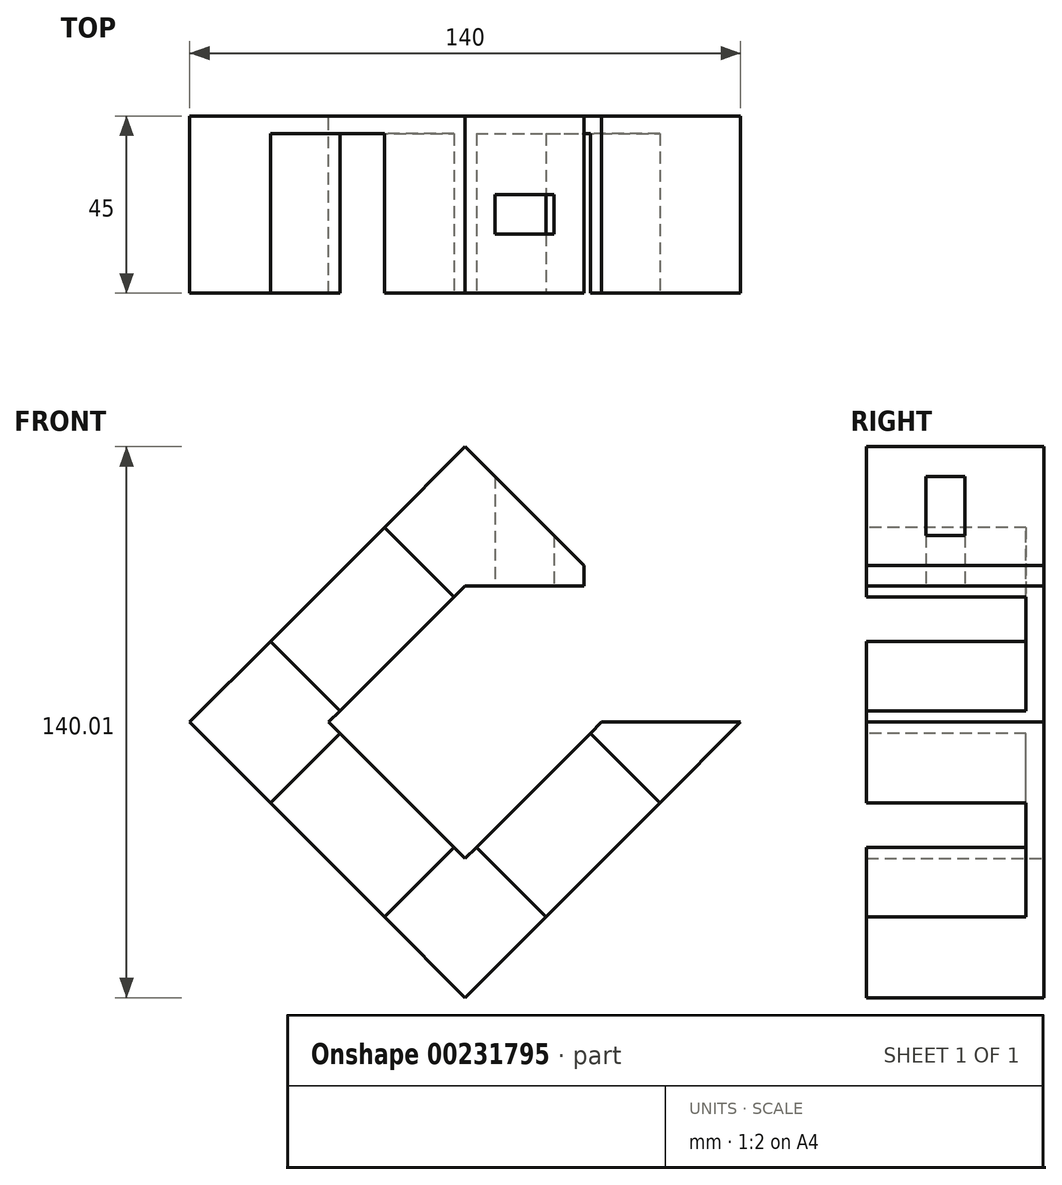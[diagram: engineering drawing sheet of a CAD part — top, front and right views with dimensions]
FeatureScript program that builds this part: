
annotation { "Feature Type Name" : "Feature", "Feature Type Description" : "" }
export const myFeature = defineFeature(function(context is Context, id is Id, definition is map)
    precondition{}
    {
        {
            var Q0;
            Q0=qCreatedBy(makeId("Front.planeOp"),FACE);
            var sketch = newSketch(context, id + "F0", { "sketchPlane" : qUnion([Q0])});
            skLineSegment(sketch, "E0", {"start": v(0, 0) * mm, "end": v(34.65, 34.65) * mm});
            skLineSegment(sketch, "E1", {"start": v(0, 0) * mm, "end": v(-34.65, 34.65) * mm});
            skLineSegment(sketch, "E2", {"start": v(-34.65, 34.65) * mm, "end": v(0, 69.3) * mm});
            skLineSegment(sketch, "E3", {"start": v(0, 69.3) * mm, "end": v(30.17, 69.3) * mm});
            skLineSegment(sketch, "E4", {"start": v(30.17, 69.3) * mm, "end": v(30.17, 74.48) * mm});
            skLineSegment(sketch, "E5", {"start": v(30.17, 74.48) * mm, "end": v(0, 104.65) * mm});
            skLineSegment(sketch, "E6", {"start": v(0, 104.65) * mm, "end": v(-70, 34.65) * mm});
            skLineSegment(sketch, "E7", {"start": v(-70, 34.65) * mm, "end": v(0, -35.36) * mm});
            skLineSegment(sketch, "E8", {"start": v(0, -35.36) * mm, "end": v(70, 34.65) * mm});
            skLineSegment(sketch, "E9", {"start": v(70, 34.65) * mm, "end": v(34.65, 34.65) * mm});
            skLineSegment(sketch, "E10", {"start": v(17.32, 17.32) * mm, "end": v(17.32, 69.3) * mm, "construction": true});
            skSolve(sketch);
        }
        {
            var Q0;
            Q0 = qSketchRegion(id + "F0", true);
            extrude(context, id + "F1", {"entities" : qUnion([Q0]), "depth" : 45 * mm});
        }
        {
            var Q0;
            Q0=makeQuery(id+"F1.opExtrude","CAP_FACE",FACE,{"disambiguationData":[OSD([sQuery(id+"F0.wireOp",EDGE,"E0"),sQuery(id+"F0.wireOp",EDGE,"E1"),sQuery(id+"F0.wireOp",EDGE,"E2"),sQuery(id+"F0.wireOp",EDGE,"E3"),sQuery(id+"F0.wireOp",EDGE,"E4"),sQuery(id+"F0.wireOp",EDGE,"E5"),sQuery(id+"F0.wireOp",EDGE,"E6"),sQuery(id+"F0.wireOp",EDGE,"E7"),sQuery(id+"F0.wireOp",EDGE,"E8"),sQuery(id+"F0.wireOp",EDGE,"E9")])],"isStart":false});
            var sketch = newSketch(context, id + "F2", { "sketchPlane" : qUnion([Q0])});
            skLineSegment(sketch, "E11", {"start": v(-49.5, 55.15) * mm, "end": v(-31.82, 37.48) * mm});
            skLineSegment(sketch, "E12", {"start": v(-31.82, 37.48) * mm, "end": v(-2.83, 66.47) * mm});
            skLineSegment(sketch, "E13", {"start": v(-2.83, 66.47) * mm, "end": v(-20.5, 84.15) * mm});
            skLineSegment(sketch, "E14", {"start": v(-20.5, 84.15) * mm, "end": v(-49.5, 55.15) * mm});
            skLineSegment(sketch, "E15", {"start": v(-31.82, 31.82) * mm, "end": v(-49.5, 14.14) * mm});
            skLineSegment(sketch, "E16", {"start": v(-49.5, 14.14) * mm, "end": v(-20.5, -14.85) * mm});
            skLineSegment(sketch, "E17", {"start": v(-20.5, -14.85) * mm, "end": v(-2.83, 2.83) * mm});
            skLineSegment(sketch, "E18", {"start": v(-2.83, 2.83) * mm, "end": v(-31.82, 31.82) * mm});
            skLineSegment(sketch, "E19", {"start": v(2.83, 2.83) * mm, "end": v(20.5, -14.85) * mm});
            skLineSegment(sketch, "E20", {"start": v(20.5, -14.85) * mm, "end": v(49.5, 14.14) * mm});
            skLineSegment(sketch, "E21", {"start": v(49.5, 14.14) * mm, "end": v(31.82, 31.82) * mm});
            skLineSegment(sketch, "E22", {"start": v(31.82, 31.82) * mm, "end": v(2.83, 2.83) * mm});
            skSolve(sketch);
        }
        {
            var Q0;
            Q0 = qSketchRegion(id + "F2", true);
            extrude(context, id + "F3", {"entities" : qUnion([Q0]), "operationType" : NewBodyOperationType.REMOVE, "oppositeDirection" : true, "depth" : 40.5 * mm});
        }
        {
            var Q0;
            Q0=makeQuery(id+"F1.opExtrude","SWEPT_FACE",FACE,{"disambiguationData":[OSD([sQuery(id+"F0.wireOp",EDGE,"E3")])]});
            var sketch = newSketch(context, id + "F4", { "sketchPlane" : qUnion([Q0])});
            skLineSegment(sketch, "E23", {"start": v(7.59, 30) * mm, "end": v(22.59, 30) * mm});
            skLineSegment(sketch, "E24", {"start": v(22.59, 30) * mm, "end": v(22.59, 20) * mm});
            skLineSegment(sketch, "E25", {"start": v(22.59, 20) * mm, "end": v(7.59, 20) * mm});
            skLineSegment(sketch, "E26", {"start": v(7.59, 20) * mm, "end": v(7.59, 30) * mm});
            skLineSegment(sketch, "E27", {"start": v(15.09, 30) * mm, "end": v(15.09, 45) * mm, "construction": true});
            skSolve(sketch);
        }
        {
            var Q0;
            Q0 = qSketchRegion(id + "F4", true);
            extrude(context, id + "F5", {"entities" : qUnion([Q0]), "operationType" : NewBodyOperationType.REMOVE, "oppositeDirection" : true, "depth" : 30 * mm});
        }
    });
